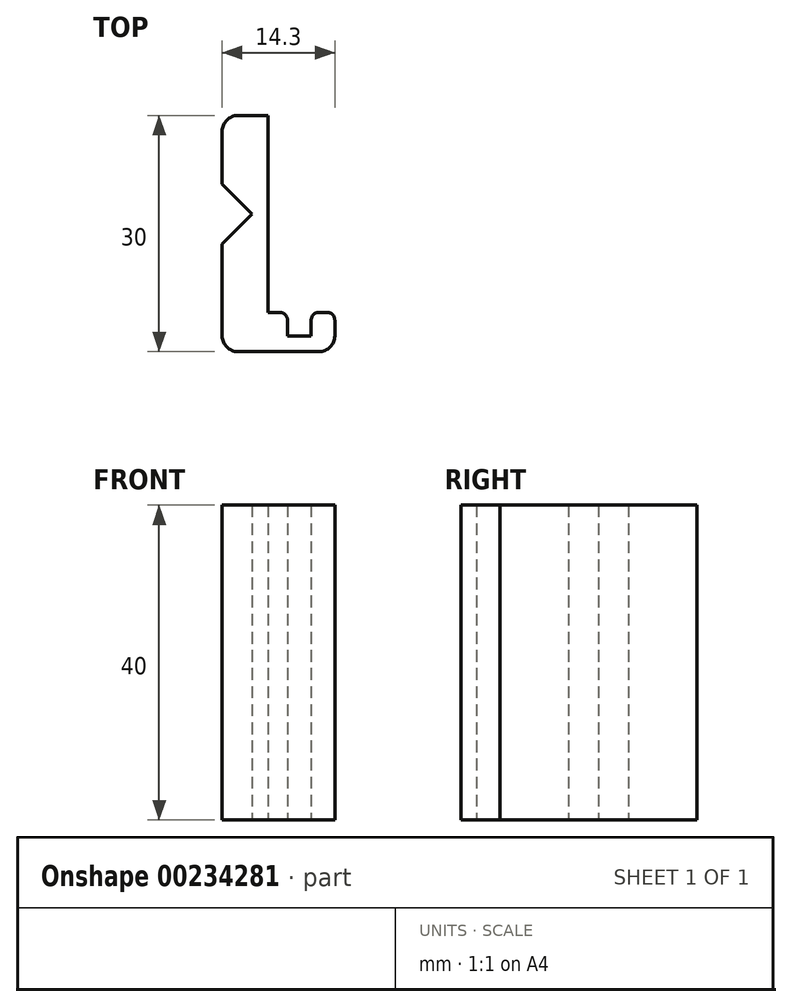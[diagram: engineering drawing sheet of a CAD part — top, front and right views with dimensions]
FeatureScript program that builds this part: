
annotation { "Feature Type Name" : "Feature", "Feature Type Description" : "" }
export const myFeature = defineFeature(function(context is Context, id is Id, definition is map)
    precondition{}
    {
        {
            var Q0;
            Q0=qCreatedBy(makeId("Top.planeOp"),FACE);
            var sketch = newSketch(context, id + "F0", { "sketchPlane" : qUnion([Q0])});
            skLineSegment(sketch, "E0", {"start": v(0, 0) * mm, "end": v(0, -25) * mm});
            skLineSegment(sketch, "E1", {"start": v(0, -25) * mm, "end": v(1.5, -25) * mm});
            skLineSegment(sketch, "E2", {"start": v(2.5, -26) * mm, "end": v(2.5, -28) * mm});
            skLineSegment(sketch, "E3", {"start": v(2.5, -28) * mm, "end": v(5.5, -28) * mm});
            skLineSegment(sketch, "E4", {"start": v(5.5, -28) * mm, "end": v(5.5, -26) * mm});
            skLineSegment(sketch, "E5", {"start": v(6.5, -25) * mm, "end": v(7.5, -25) * mm});
            skLineSegment(sketch, "E6", {"start": v(8.5, -26) * mm, "end": v(8.5, -28) * mm});
            skLineSegment(sketch, "E7", {"start": v(6.5, -30) * mm, "end": v(0, -30) * mm});
            skLineSegment(sketch, "E8", {"start": v(-23.9, -12.5) * mm, "end": v(0, -12.5) * mm, "construction": true});
            skPoint(sketch, "E8.startSnap0", {"position": v(0, -12.5) * mm});
            skLineSegment(sketch, "E9", {"start": v(-3.8, 0) * mm, "end": v(0, 0) * mm});
            skLineSegment(sketch, "E10", {"start": v(-2, -12.5) * mm, "end": v(-5.8, -8.7) * mm});
            skLineSegment(sketch, "E11", {"start": v(-5.8, -8.7) * mm, "end": v(-5.8, -2) * mm});
            skLineSegment(sketch, "E12.MirrorCS", {"start": v(-2, -12.5) * mm, "end": v(-5.8, -16.3) * mm});
            skLineSegment(sketch, "E13.MirrorCS", {"start": v(-5.8, -16.3) * mm, "end": v(-5.8, -25) * mm});
            skLineSegment(sketch, "E14", {"start": v(0, -30) * mm, "end": v(-3.8, -30) * mm});
            skLineSegment(sketch, "E15", {"start": v(-5.8, -28) * mm, "end": v(-5.8, -25) * mm});
            skPoint(sketch, "E16.visualSharp", {"position": v(-5.8, 0) * mm});
            skArc(sketch, "E16.filletArc", {"start": v(-3.8, 0) * mm, "mid": v(-5.21, -0.59) * mm, "end": v(-5.8, -2) * mm});
            skPoint(sketch, "E17.visualSharp", {"position": v(-5.8, -30) * mm});
            skArc(sketch, "E17.filletArc", {"start": v(-5.8, -28) * mm, "mid": v(-5.21, -29.41) * mm, "end": v(-3.8, -30) * mm});
            skPoint(sketch, "E18.visualSharp", {"position": v(8.5, -30) * mm});
            skArc(sketch, "E18.filletArc", {"start": v(6.5, -30) * mm, "mid": v(7.91, -29.41) * mm, "end": v(8.5, -28) * mm});
            skPoint(sketch, "E19.visualSharp", {"position": v(2.5, -25) * mm});
            skArc(sketch, "E19.filletArc", {"start": v(2.5, -26) * mm, "mid": v(2.2, -25.3) * mm, "end": v(1.5, -25) * mm});
            skPoint(sketch, "E20.visualSharp", {"position": v(5.5, -25) * mm});
            skArc(sketch, "E20.filletArc", {"start": v(6.5, -25) * mm, "mid": v(5.8, -25.3) * mm, "end": v(5.5, -26) * mm});
            skPoint(sketch, "E21.visualSharp", {"position": v(8.5, -25) * mm});
            skArc(sketch, "E21.filletArc", {"start": v(8.5, -26) * mm, "mid": v(8.2, -25.3) * mm, "end": v(7.5, -25) * mm});
            skSolve(sketch);
        }
        {
            var Q0;
            Q0=makeQuery(id+"F0.imprint","IMPRINT",FACE,{"disambiguationData":[TD([[makeQuery(id+"F0.imprint","IMPRINT",EDGE,{"derivedFrom":sQuery(id+"F0.wireOp",EDGE,"E0")}),-1.0]])]});
            extrude(context, id + "F1", {"entities" : qUnion([Q0]), "depth" : 40 * mm});
        }
    });
